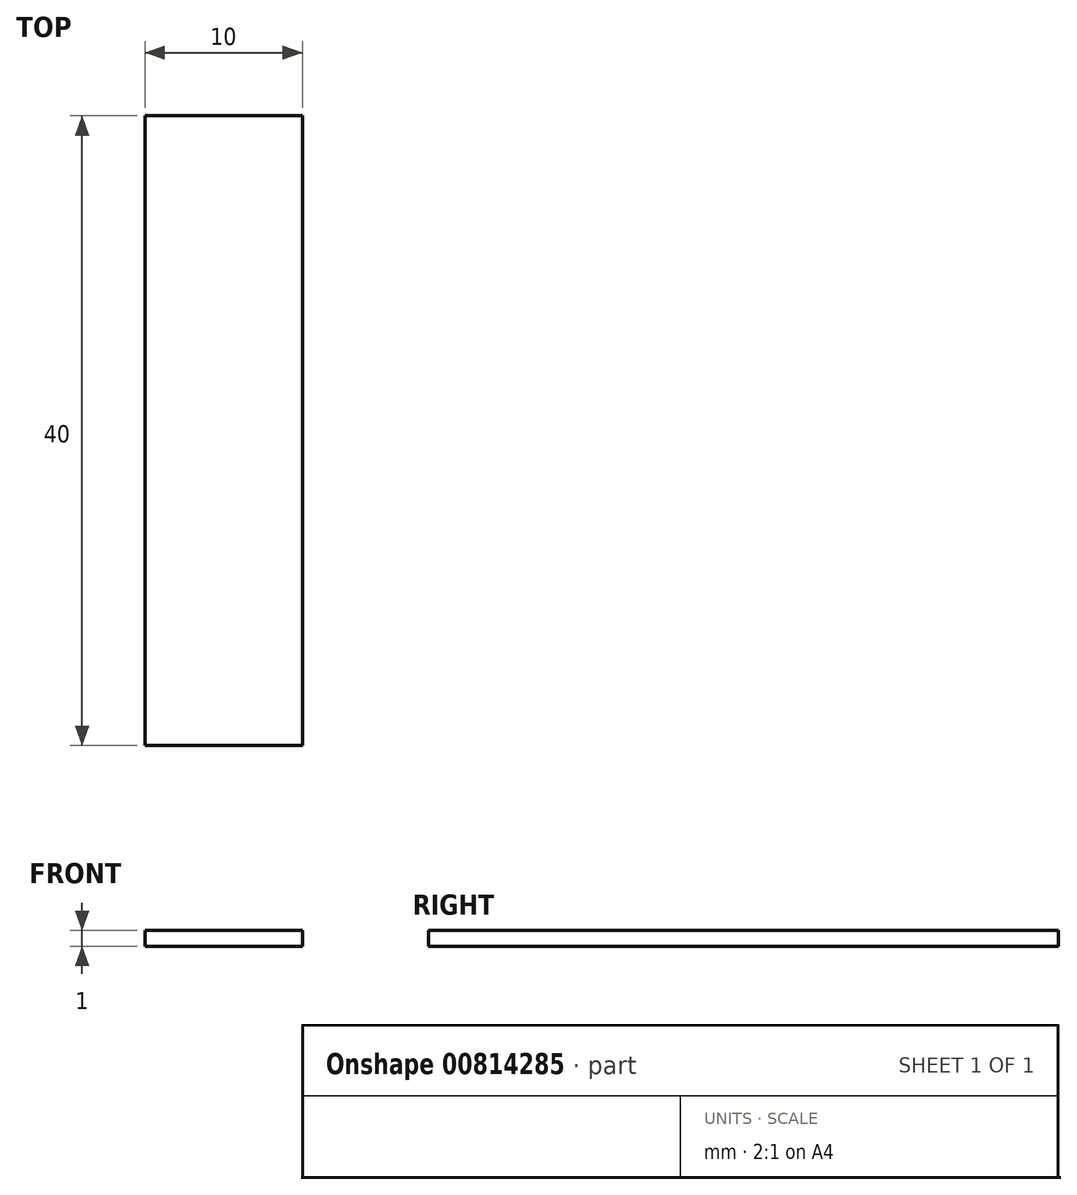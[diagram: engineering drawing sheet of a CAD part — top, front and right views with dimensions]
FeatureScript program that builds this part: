
annotation { "Feature Type Name" : "Feature", "Feature Type Description" : "" }
export const myFeature = defineFeature(function(context is Context, id is Id, definition is map)
    precondition{}
    {
        {
            var Q0;
            Q0=qCreatedBy(makeId("Front.planeOp"),FACE);
            var sketch = newSketch(context, id + "F0", { "sketchPlane" : qUnion([Q0])});
            skPoint(sketch, "E0.middle", {"position": v(0, 0) * mm});
            skLineSegment(sketch, "E1.bottom", {"start": v(-0.5, 3.5) * mm, "end": v(9.5, 3.5) * mm});
            skLineSegment(sketch, "E1.top", {"start": v(-0.5, 2.5) * mm, "end": v(9.5, 2.5) * mm});
            skLineSegment(sketch, "E1.left", {"start": v(-0.5, 3.5) * mm, "end": v(-0.5, 2.5) * mm});
            skLineSegment(sketch, "E1.right", {"start": v(9.5, 3.5) * mm, "end": v(9.5, 2.5) * mm});
            skSolve(sketch);
        }
        {
            var Q0;
            Q0=makeQuery(id+"F0.imprint","IMPRINT",FACE,{"disambiguationData":[TD([[makeQuery(id+"F0.imprint","IMPRINT",EDGE,{"derivedFrom":sQuery(id+"F0.wireOp",EDGE,"E1.bottom")}),-1.0]])]});
            var Q1;
            Q1=makeQuery(id+"F0.imprint","IMPRINT",FACE,{"disambiguationData":[TD([[makeQuery(id+"F0.imprint","IMPRINT",EDGE,{"derivedFrom":sQuery(id+"F0.wireOp",EDGE,"E0.bottom")}),1.0]])]});
            extrude(context, id + "F1", {"entities" : qUnion([Q0, Q1]), "depth" : 40 * mm, "offsetDistance" : 25 * mm});
        }
    });
